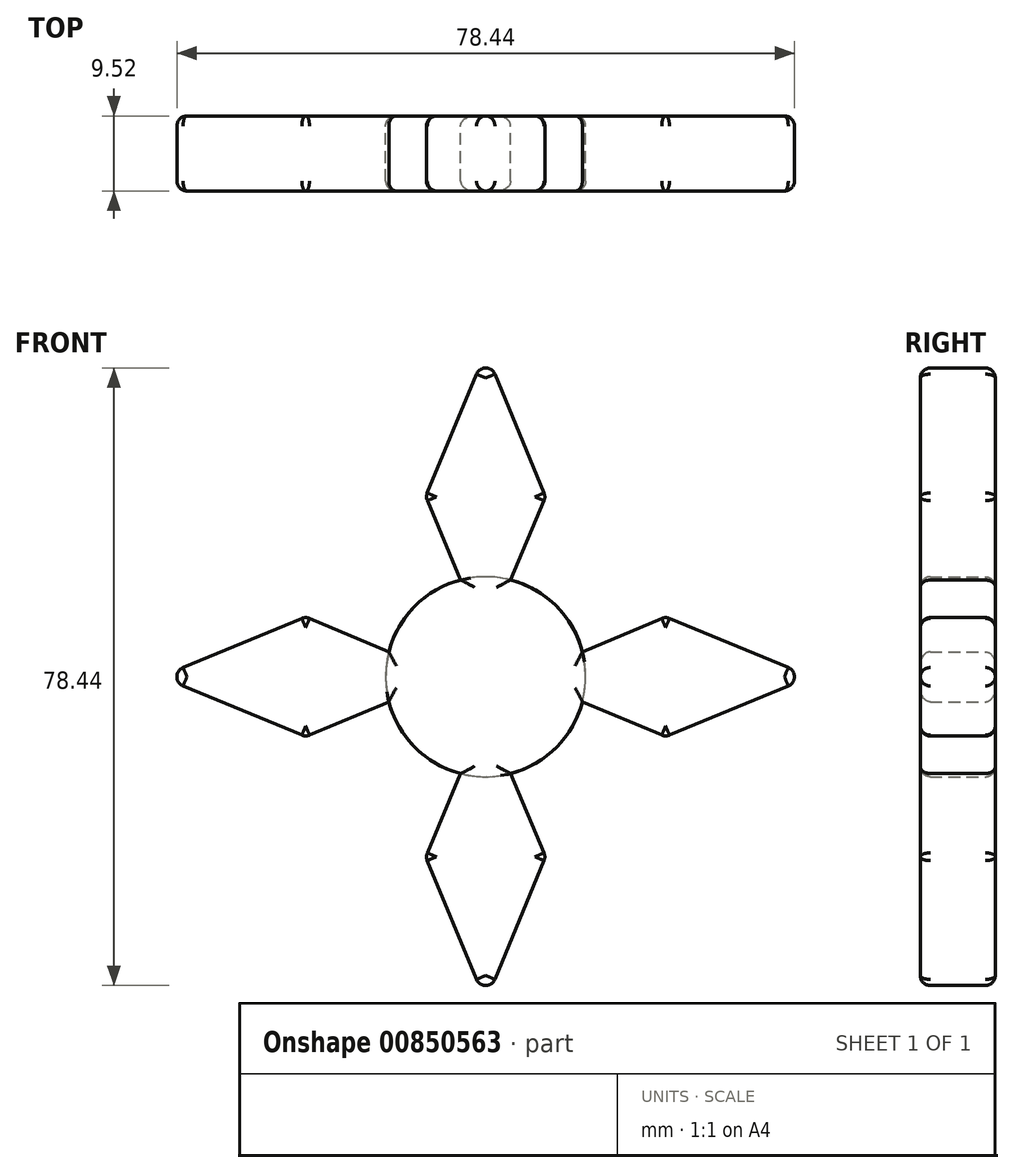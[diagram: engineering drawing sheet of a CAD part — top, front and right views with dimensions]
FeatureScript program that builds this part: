
annotation { "Feature Type Name" : "Feature", "Feature Type Description" : "" }
export const myFeature = defineFeature(function(context is Context, id is Id, definition is map)
    precondition{}
    {
        {
            var Q0;
            Q0=qCreatedBy(makeId("Front.planeOp"),FACE);
            var sketch = newSketch(context, id + "F0", { "sketchPlane" : qUnion([Q0])});
            skCircle(sketch, "E0", {"center": v(0, 0) * mm, "radius": 12.7 * mm});
            skSolve(sketch);
        }
        {
            var Q0;
            Q0=makeQuery(id+"F0.imprint","IMPRINT",FACE,{"disambiguationData":[TD([[makeQuery(id+"F0.imprint","IMPRINT",EDGE,{"derivedFrom":sQuery(id+"F0.wireOp",EDGE,"E0")}),1.0]])]});
            extrude(context, id + "F1", {"entities" : qUnion([Q0]), "depth" : 9.52 * mm, "offsetDistance" : 25.4 * mm, "symmetric" : true});
        }
        {
            var Q0;
            Q0=qCreatedBy(makeId("Front.planeOp"),FACE);
            var sketch = newSketch(context, id + "F2", { "sketchPlane" : qUnion([Q0])});
            skLineSegment(sketch, "E1", {"start": v(0, 40.86) * mm, "end": v(0, -5.88) * mm, "construction": true});
            skLineSegment(sketch, "E2", {"start": v(-3.17, 12.3) * mm, "end": v(-7.62, 22.86) * mm});
            skLineSegment(sketch, "E3", {"start": v(-7.62, 22.86) * mm, "end": v(0, 41.28) * mm});
            skLineSegment(sketch, "E4", {"start": v(-16.85, 22.86) * mm, "end": v(19.6, 22.86) * mm, "construction": true});
            skLineSegment(sketch, "E5", {"start": v(0, 41.28) * mm, "end": v(7.62, 22.86) * mm});
            skLineSegment(sketch, "E6", {"start": v(7.62, 22.86) * mm, "end": v(3.17, 12.3) * mm});
            skLineSegment(sketch, "E7", {"start": v(-3.17, 12.3) * mm, "end": v(3.18, 12.3) * mm});
            skSolve(sketch);
        }
        {
            var Q0;
            Q0=makeQuery(id+"F2.imprint","IMPRINT",FACE,{"disambiguationData":[TD([[makeQuery(id+"F2.imprint","IMPRINT",EDGE,{"derivedFrom":sQuery(id+"F2.wireOp",EDGE,"E2")}),-1.0]])]});
            extrude(context, id + "F3", {"entities" : qUnion([Q0]), "operationType" : NewBodyOperationType.ADD, "depth" : 9.52 * mm, "offsetDistance" : 25.4 * mm, "symmetric" : true});
        }
        {
            var Q0;
            Q0=qCreatedBy(makeId("Top.planeOp"),FACE);
            var sketch = newSketch(context, id + "F4", { "sketchPlane" : qUnion([Q0])});
            skLineSegment(sketch, "E8", {"start": v(0, 43.35) * mm, "end": v(0, -35.57) * mm, "construction": true});
            skSolve(sketch);
        }
        {
            var Q0;
            Q0=makeQuery(id+"F3.boolean.opBoolean","MERGE",FACE,{"derivedFrom":[makeQuery(id+"F1.opExtrude","CAP_FACE",FACE,{"disambiguationData":[OSD([sQuery(id+"F0.wireOp",EDGE,"E0")])],"isStart":false}),makeQuery(id+"F3.opExtrude","CAP_FACE",FACE,{"disambiguationData":[OSD([sQuery(id+"F2.wireOp",EDGE,"E2"),sQuery(id+"F2.wireOp",EDGE,"E3"),sQuery(id+"F2.wireOp",EDGE,"E5"),sQuery(id+"F2.wireOp",EDGE,"E6"),sQuery(id+"F2.wireOp",EDGE,"E7")])],"isStart":false})]});
            var sketch = newSketch(context, id + "F5", { "sketchPlane" : qUnion([Q0])});
            skText(sketch, "E9", { "text": "NORA", "fontName": "OpenSans-Regular.ttf"});
            const initialGuessF5  = {"E9": [-0.00537, 0.0219, 1, 0, 0.00259]};
            skSetInitialGuess(sketch, initialGuessF5);
            skSolve(sketch);
        }
        {
            var Q0;
            Q0=qConstructionFilter(qBodyType(qCreatedBy(id+"F5",EDGE),BodyType.WIRE),ConstructionObject.NO);
            extrude(context, id + "F6", {"bodyType" : ToolBodyType.SURFACE, "surfaceEntities" : qUnion([Q0]), "depth" : 0.25 * mm, "offsetDistance" : 25.4 * mm});
        }
        {
            var Q0;
            Q0=makeQuery(id+"F1.opExtrude","SWEPT_BODY",BODY,{"disambiguationData":[OSD([sQuery(id+"F0.wireOp",EDGE,"E0")])]});
            var Q1;
            Q1=sQuery(id+"F4.wireOp",EDGE,"E8");
            circularPattern(context, id + "F7", {"entities" : qUnion([Q0]), "axis" : qUnion([Q1]), "angle" : 360 * degree, "instanceCount" : 4, "equalSpace" : true});
        }
        {
            var Q0;
            Q0=makeQuery(id+"F7.opPattern","COPY",FACE,{"derivedFrom":makeQuery(id+"F3.boolean.opBoolean","MERGE",FACE,{"derivedFrom":[makeQuery(id+"F1.opExtrude","CAP_FACE",FACE,{"disambiguationData":[OSD([sQuery(id+"F0.wireOp",EDGE,"E0")])],"isStart":false}),makeQuery(id+"F3.opExtrude","CAP_FACE",FACE,{"disambiguationData":[OSD([sQuery(id+"F2.wireOp",EDGE,"E2"),sQuery(id+"F2.wireOp",EDGE,"E3"),sQuery(id+"F2.wireOp",EDGE,"E5"),sQuery(id+"F2.wireOp",EDGE,"E6"),sQuery(id+"F2.wireOp",EDGE,"E7")])],"isStart":false})]}),"instanceName":"3"});
            var Q1;
            Q1=makeQuery(id+"F3.boolean.opBoolean","MERGE",FACE,{"derivedFrom":[makeQuery(id+"F1.opExtrude","CAP_FACE",FACE,{"disambiguationData":[OSD([sQuery(id+"F0.wireOp",EDGE,"E0")])],"isStart":false}),makeQuery(id+"F3.opExtrude","CAP_FACE",FACE,{"disambiguationData":[OSD([sQuery(id+"F2.wireOp",EDGE,"E2"),sQuery(id+"F2.wireOp",EDGE,"E3"),sQuery(id+"F2.wireOp",EDGE,"E5"),sQuery(id+"F2.wireOp",EDGE,"E6"),sQuery(id+"F2.wireOp",EDGE,"E7")])],"isStart":false})]});
            var Q2;
            Q2=makeQuery(id+"F7.opPattern","COPY",FACE,{"derivedFrom":makeQuery(id+"F3.boolean.opBoolean","MERGE",FACE,{"derivedFrom":[makeQuery(id+"F1.opExtrude","CAP_FACE",FACE,{"disambiguationData":[OSD([sQuery(id+"F0.wireOp",EDGE,"E0")])],"isStart":false}),makeQuery(id+"F3.opExtrude","CAP_FACE",FACE,{"disambiguationData":[OSD([sQuery(id+"F2.wireOp",EDGE,"E2"),sQuery(id+"F2.wireOp",EDGE,"E3"),sQuery(id+"F2.wireOp",EDGE,"E5"),sQuery(id+"F2.wireOp",EDGE,"E6"),sQuery(id+"F2.wireOp",EDGE,"E7")])],"isStart":false})]}),"instanceName":"1"});
            var Q3;
            Q3=makeQuery(id+"F7.opPattern","COPY",FACE,{"derivedFrom":makeQuery(id+"F3.boolean.opBoolean","MERGE",FACE,{"derivedFrom":[makeQuery(id+"F1.opExtrude","CAP_FACE",FACE,{"disambiguationData":[OSD([sQuery(id+"F0.wireOp",EDGE,"E0")])],"isStart":false}),makeQuery(id+"F3.opExtrude","CAP_FACE",FACE,{"disambiguationData":[OSD([sQuery(id+"F2.wireOp",EDGE,"E2"),sQuery(id+"F2.wireOp",EDGE,"E3"),sQuery(id+"F2.wireOp",EDGE,"E5"),sQuery(id+"F2.wireOp",EDGE,"E6"),sQuery(id+"F2.wireOp",EDGE,"E7")])],"isStart":false})]}),"instanceName":"2"});
            var Q4;
            Q4=makeQuery(id+"F3.boolean.opBoolean","MERGE",FACE,{"derivedFrom":[makeQuery(id+"F1.opExtrude","CAP_FACE",FACE,{"disambiguationData":[OSD([sQuery(id+"F0.wireOp",EDGE,"E0")])],"isStart":true}),makeQuery(id+"F3.opExtrude","CAP_FACE",FACE,{"disambiguationData":[OSD([sQuery(id+"F2.wireOp",EDGE,"E2"),sQuery(id+"F2.wireOp",EDGE,"E3"),sQuery(id+"F2.wireOp",EDGE,"E5"),sQuery(id+"F2.wireOp",EDGE,"E6"),sQuery(id+"F2.wireOp",EDGE,"E7")])],"isStart":true})]});
            var Q5;
            Q5=makeQuery(id+"F7.opPattern","COPY",FACE,{"derivedFrom":makeQuery(id+"F3.boolean.opBoolean","MERGE",FACE,{"derivedFrom":[makeQuery(id+"F1.opExtrude","CAP_FACE",FACE,{"disambiguationData":[OSD([sQuery(id+"F0.wireOp",EDGE,"E0")])],"isStart":true}),makeQuery(id+"F3.opExtrude","CAP_FACE",FACE,{"disambiguationData":[OSD([sQuery(id+"F2.wireOp",EDGE,"E2"),sQuery(id+"F2.wireOp",EDGE,"E3"),sQuery(id+"F2.wireOp",EDGE,"E5"),sQuery(id+"F2.wireOp",EDGE,"E6"),sQuery(id+"F2.wireOp",EDGE,"E7")])],"isStart":true})]}),"instanceName":"2"});
            var Q6;
            Q6=makeQuery(id+"F7.opPattern","COPY",FACE,{"derivedFrom":makeQuery(id+"F3.boolean.opBoolean","MERGE",FACE,{"derivedFrom":[makeQuery(id+"F1.opExtrude","CAP_FACE",FACE,{"disambiguationData":[OSD([sQuery(id+"F0.wireOp",EDGE,"E0")])],"isStart":true}),makeQuery(id+"F3.opExtrude","CAP_FACE",FACE,{"disambiguationData":[OSD([sQuery(id+"F2.wireOp",EDGE,"E2"),sQuery(id+"F2.wireOp",EDGE,"E3"),sQuery(id+"F2.wireOp",EDGE,"E5"),sQuery(id+"F2.wireOp",EDGE,"E6"),sQuery(id+"F2.wireOp",EDGE,"E7")])],"isStart":true})]}),"instanceName":"3"});
            var Q7;
            Q7=makeQuery(id+"F7.opPattern","COPY",FACE,{"derivedFrom":makeQuery(id+"F3.boolean.opBoolean","MERGE",FACE,{"derivedFrom":[makeQuery(id+"F1.opExtrude","CAP_FACE",FACE,{"disambiguationData":[OSD([sQuery(id+"F0.wireOp",EDGE,"E0")])],"isStart":true}),makeQuery(id+"F3.opExtrude","CAP_FACE",FACE,{"disambiguationData":[OSD([sQuery(id+"F2.wireOp",EDGE,"E2"),sQuery(id+"F2.wireOp",EDGE,"E3"),sQuery(id+"F2.wireOp",EDGE,"E5"),sQuery(id+"F2.wireOp",EDGE,"E6"),sQuery(id+"F2.wireOp",EDGE,"E7")])],"isStart":true})]}),"instanceName":"1"});
            fillet(context, id + "F8", {"entities" : qUnion([Q0, Q1, Q2, Q3, Q4, Q5, Q6, Q7]), "radius" : 1.27 * mm, "tangentPropagation" : true, "allowEdgeOverflow" : false});
        }
        {
            var Q0;
            Q0=makeQuery(id+"F7.opPattern","COPY",EDGE,{"derivedFrom":makeQuery(id+"F3.opExtrude","SWEPT_EDGE",EDGE,{"disambiguationData":[OSD([sQuery(id+"F2.wireOp",EDGE,"E3"),sQuery(id+"F2.wireOp",EDGE,"E5")])]}),"instanceName":"1"});
            var Q1;
            Q1=makeQuery(id+"F7.opPattern","COPY",EDGE,{"derivedFrom":makeQuery(id+"F3.opExtrude","SWEPT_EDGE",EDGE,{"disambiguationData":[OSD([sQuery(id+"F2.wireOp",EDGE,"E5"),sQuery(id+"F2.wireOp",EDGE,"E6")])]}),"instanceName":"1"});
            var Q2;
            Q2=makeQuery(id+"F3.opExtrude","SWEPT_EDGE",EDGE,{"disambiguationData":[OSD([sQuery(id+"F2.wireOp",EDGE,"E2"),sQuery(id+"F2.wireOp",EDGE,"E7")])]});
            var Q3;
            Q3=makeQuery(id+"F7.opPattern","COPY",EDGE,{"derivedFrom":makeQuery(id+"F3.opExtrude","SWEPT_EDGE",EDGE,{"disambiguationData":[OSD([sQuery(id+"F2.wireOp",EDGE,"E6"),sQuery(id+"F2.wireOp",EDGE,"E7")])]}),"instanceName":"1"});
            var Q4;
            Q4=makeQuery(id+"F3.opExtrude","SWEPT_EDGE",EDGE,{"disambiguationData":[OSD([sQuery(id+"F2.wireOp",EDGE,"E2"),sQuery(id+"F2.wireOp",EDGE,"E3")])]});
            var Q5;
            Q5=makeQuery(id+"F3.opExtrude","SWEPT_EDGE",EDGE,{"disambiguationData":[OSD([sQuery(id+"F2.wireOp",EDGE,"E3"),sQuery(id+"F2.wireOp",EDGE,"E5")])]});
            var Q6;
            Q6=makeQuery(id+"F3.opExtrude","SWEPT_EDGE",EDGE,{"disambiguationData":[OSD([sQuery(id+"F2.wireOp",EDGE,"E5"),sQuery(id+"F2.wireOp",EDGE,"E6")])]});
            var Q7;
            Q7=makeQuery(id+"F3.opExtrude","SWEPT_EDGE",EDGE,{"disambiguationData":[OSD([sQuery(id+"F2.wireOp",EDGE,"E6"),sQuery(id+"F2.wireOp",EDGE,"E7")])]});
            var Q8;
            Q8=makeQuery(id+"F7.opPattern","COPY",EDGE,{"derivedFrom":makeQuery(id+"F3.opExtrude","SWEPT_EDGE",EDGE,{"disambiguationData":[OSD([sQuery(id+"F2.wireOp",EDGE,"E2"),sQuery(id+"F2.wireOp",EDGE,"E7")])]}),"instanceName":"3"});
            var Q9;
            Q9=makeQuery(id+"F7.opPattern","COPY",EDGE,{"derivedFrom":makeQuery(id+"F3.opExtrude","SWEPT_EDGE",EDGE,{"disambiguationData":[OSD([sQuery(id+"F2.wireOp",EDGE,"E2"),sQuery(id+"F2.wireOp",EDGE,"E3")])]}),"instanceName":"3"});
            var Q10;
            Q10=makeQuery(id+"F7.opPattern","COPY",EDGE,{"derivedFrom":makeQuery(id+"F3.opExtrude","SWEPT_EDGE",EDGE,{"disambiguationData":[OSD([sQuery(id+"F2.wireOp",EDGE,"E3"),sQuery(id+"F2.wireOp",EDGE,"E5")])]}),"instanceName":"3"});
            var Q11;
            Q11=makeQuery(id+"F7.opPattern","COPY",EDGE,{"derivedFrom":makeQuery(id+"F3.opExtrude","SWEPT_EDGE",EDGE,{"disambiguationData":[OSD([sQuery(id+"F2.wireOp",EDGE,"E5"),sQuery(id+"F2.wireOp",EDGE,"E6")])]}),"instanceName":"3"});
            var Q12;
            Q12=makeQuery(id+"F7.opPattern","COPY",EDGE,{"derivedFrom":makeQuery(id+"F3.opExtrude","SWEPT_EDGE",EDGE,{"disambiguationData":[OSD([sQuery(id+"F2.wireOp",EDGE,"E6"),sQuery(id+"F2.wireOp",EDGE,"E7")])]}),"instanceName":"3"});
            var Q13;
            Q13=makeQuery(id+"F7.opPattern","COPY",EDGE,{"derivedFrom":makeQuery(id+"F3.opExtrude","SWEPT_EDGE",EDGE,{"disambiguationData":[OSD([sQuery(id+"F2.wireOp",EDGE,"E2"),sQuery(id+"F2.wireOp",EDGE,"E7")])]}),"instanceName":"2"});
            var Q14;
            Q14=makeQuery(id+"F7.opPattern","COPY",EDGE,{"derivedFrom":makeQuery(id+"F3.opExtrude","SWEPT_EDGE",EDGE,{"disambiguationData":[OSD([sQuery(id+"F2.wireOp",EDGE,"E2"),sQuery(id+"F2.wireOp",EDGE,"E3")])]}),"instanceName":"2"});
            var Q15;
            Q15=makeQuery(id+"F7.opPattern","COPY",EDGE,{"derivedFrom":makeQuery(id+"F3.opExtrude","SWEPT_EDGE",EDGE,{"disambiguationData":[OSD([sQuery(id+"F2.wireOp",EDGE,"E3"),sQuery(id+"F2.wireOp",EDGE,"E5")])]}),"instanceName":"2"});
            var Q16;
            Q16=makeQuery(id+"F7.opPattern","COPY",EDGE,{"derivedFrom":makeQuery(id+"F3.opExtrude","SWEPT_EDGE",EDGE,{"disambiguationData":[OSD([sQuery(id+"F2.wireOp",EDGE,"E5"),sQuery(id+"F2.wireOp",EDGE,"E6")])]}),"instanceName":"2"});
            var Q17;
            Q17=makeQuery(id+"F7.opPattern","COPY",EDGE,{"derivedFrom":makeQuery(id+"F3.opExtrude","SWEPT_EDGE",EDGE,{"disambiguationData":[OSD([sQuery(id+"F2.wireOp",EDGE,"E6"),sQuery(id+"F2.wireOp",EDGE,"E7")])]}),"instanceName":"2"});
            var Q18;
            Q18=makeQuery(id+"F7.opPattern","COPY",EDGE,{"derivedFrom":makeQuery(id+"F3.opExtrude","SWEPT_EDGE",EDGE,{"disambiguationData":[OSD([sQuery(id+"F2.wireOp",EDGE,"E2"),sQuery(id+"F2.wireOp",EDGE,"E7")])]}),"instanceName":"1"});
            var Q19;
            Q19=makeQuery(id+"F7.opPattern","COPY",EDGE,{"derivedFrom":makeQuery(id+"F3.opExtrude","SWEPT_EDGE",EDGE,{"disambiguationData":[OSD([sQuery(id+"F2.wireOp",EDGE,"E2"),sQuery(id+"F2.wireOp",EDGE,"E3")])]}),"instanceName":"1"});
            fillet(context, id + "F9", {"entities" : qUnion([Q0, Q1, Q2, Q3, Q4, Q5, Q6, Q7, Q8, Q9, Q10, Q11, Q12, Q13, Q14, Q15, Q16, Q17, Q18, Q19]), "radius" : 1.27 * mm, "tangentPropagation" : true, "allowEdgeOverflow" : false});
        }
    });
